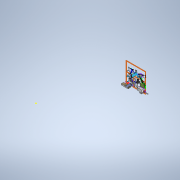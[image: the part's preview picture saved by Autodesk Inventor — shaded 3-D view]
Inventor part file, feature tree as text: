
AUTODESK INVENTOR PART (.ipt)
format: ipt  version: 2022 (Build 260153000, 153)  size: 390,144 bytes
history: native  units: in
note: dims shown in document units (in); Inventor stores cm internally (conversion verified against a paired STEP export)
features: extrude x29, sketch x1, fillet x1
ambient origin geometry x8: Origin, YZ Plane, XZ Plane, XY Plane, X Axis, Y Axis, Z Axis, Center Point
bodies: Solide1 (feature_tree)
feature tree (31):
  sketch  "Esquisse1"
  extrude  "Extrusion1"  Depth=1.9685in TaperAngle=0.0deg
  extrude  "Extrusion2"  Depth=1.5748in TaperAngle=0.0deg
  extrude  "Extrusion3"  Depth=0.7874in TaperAngle=0.0deg
  extrude  "Extrusion4"  Depth=0.3937in
  extrude  "Extrusion5"  Depth=0.3937in
  extrude  "Extrusion6"  Depth=0.3937in
  extrude  "Extrusion10"  Depth=1.5748in TaperAngle=0.0deg
  extrude  "Extrusion12"  Depth=1.5748in TaperAngle=0.0deg
  extrude  "Extrusion13"  Depth=3.937in TaperAngle=0.0deg
  extrude  "Extrusion14"  Depth=0.1181in
  extrude  "Extrusion15"  Depth=0.1181in
  extrude  "Extrusion16"  Depth=1.5748in TaperAngle=0.0deg
  extrude  "Extrusion17"  Depth=2.2835in TaperAngle=0.0deg
  extrude  "Extrusion18"  Depth=0.5906in TaperAngle=0.0deg
  extrude  "Extrusion19"  Depth=0.7874in TaperAngle=0.0deg
  extrude  "Extrusion20"  Depth=0.5906in TaperAngle=0.0deg
  extrude  "Extrusion21"  Depth=0.9921in TaperAngle=0.0deg
  extrude  "Extrusion22"  Depth=0.5906in TaperAngle=0.0deg
  extrude  "Extrusion23"  Depth=0.9921in TaperAngle=0.0deg
  extrude  "Extrusion24"  Depth=2.4646in TaperAngle=0.0deg
  extrude  "Extrusion25"  Depth=0.3937in TaperAngle=0.0deg
  extrude  "Extrusion26"  Depth=4.3307in TaperAngle=0.0deg
  fillet  "Congé1"  Radius=4.3307in
  extrude  "Extrusion27"  Depth=1.1811in TaperAngle=0.0deg
  extrude  "Extrusion28"  Depth=0.9843in TaperAngle=0.0deg
  extrude  "Extrusion29"  Depth=0.3937in
  extrude  "Extrusion30"  Depth=0.3937in
  extrude  "Extrusion31"  Depth=2.0315in TaperAngle=0.0deg
  extrude  "Extrusion32"  Depth=1.3386in TaperAngle=0.0deg
  extrude  "Extrusion33"  Depth=0.5906in
